# Revit family: Clevertronics_ARGO-600-LP
name_source: partatom
category: Lighting Fixtures
units: mm (PartAtom-declared; Revit-internal decimal feet)

## family parameters
Cut with Voids When Loaded = No
Host = Face
Light Source = Yes
Part Type = Normal
Room Calculation Point = No
Round Connector Dimension = Use Diameter
Shared = No

## types (5) — shared parameters
Clevertronics_240V Driver = 1330086-A - 240V Driver
Clevertronics_240V LED Strip = 8002848 - LED Strip
Clevertronics_AS2293 Classification = C0=D40 C90=D25
Clevertronics_Applicable Standards = AS/NZS3820, CISPR15, AS/NZS2293.3
Clevertronics_Battery = 3.2V 3200mAh
Clevertronics_Battery Type = Lithium Iron Phosphate
Clevertronics_Charger Method = Intelligent current limited constant voltage
Clevertronics_Construction = Polycarbonate Base and Diffuser with Captive Stainless-Steel Clips (SS301)
Clevertronics_Diffuser = Polycarbonate
Clevertronics_Driver/Ballast = LED Driver – 20w Stallion
Clevertronics_Height = 88 mm  [stored 0.288714 ft]
Clevertronics_IK Rating = IK08
Clevertronics_IP Rating = IP65
Clevertronics_Length = 655 mm  [stored 2.14895 ft]
Clevertronics_Material = Clevertronics_Plycarbonate Base
Clevertronics_Mounting = Surface mount
Clevertronics_Operating Mode = Sustained
Clevertronics_Operating Temperature = 0˚C to 40˚C
Clevertronics_Operating Voltage = 240V AC; 50Hz
Clevertronics_Replacement Battery = 1550050 - Battery
Clevertronics_Weight = 1.5 kg
Clevertronics_Width = 121 mm  [stored 0.396982 ft]
Color Filter = 16777215
Default Elevation = 6500 mm  [stored 21.3255 ft]
Dimming Lamp Color Temperature Shift = <None>
Lamp = Dual LED strip module, 3,000K warm white, 5,700K cool white, 
50,000h life [L70/B50 Ta 40°C], Ra>80
Manufacturer = Clevertronics
Photometric Web File = ARGO-600-SEN-LP_IESR_E_693-7_20200803-01.ies
Tilt Angle = -90.00°
zero-valued in all types: Clevertronics_Annotation Size

## per-type parameters (varying)
| type | Apparent Load | Clevertronics_Emergency Driver | Clevertronics_MIC Number | Clevertronics_Power Consumption | Clevertronics_Product Description | Clevertronics_Testing Node | Clevertronics_Testing System | Clevertronics_Total Lumen Output | Description | Model |
| ARGO-600-LP AUB02320450001 | 21 VA | AUM02370080001 CLIFE-PRO-CKIT-NP-335 - Driver Pack | AUB02320450001 | 21W | LP Premium ARGO 600mm LED Weatherproof Emergency Batten with Integral 
Battery and Switchable Colour, Enabled with Clevertest Plus |  | Clevertest Plus Enabled (Not activated by default) |  | LP Premium ARGO 600mm LED Weatherproof Emergency Batten with Integral 
Battery and Switchable Colour, Enabled with Clevertest Plus | ARGO-600-LP |
| ARGO-600-LP-HV  AUB02820540001 | 22 VA | AUM02870060001 CLIFE-PRO-CKIT-HV-NP-335 - Driver Pack | AUB02820540001 | 22W | LP Premium ARGO 600mm LED Weatherproof Emergency Batten with Integral 
Battery and Switchable Colour
LP Premium ARGO 600mm LED Weatherproof Emergency Batten with Integral 
Battery and Switchable Colour
LP Premium ARGO 600mm LED Weatherproof Emergency Batten with Integral 
Battery and Switchable Colour
LP Premium ARGO 600mm LED Weatherproof Emergency Batten with Integral 
Battery and Switchable Colour | 8003191 - RF Node | Zoneworks XT HIVE (RF) |  | LP Premium ARGO 600mm LED Weatherproof Emergency Batten with Integral 
Battery and Switchable Colour | ARGO-600-LP-HV |
| ARGO-600-LP-HVG  AUB02920050001 | 22 VA | AUM02970070001 CLIFE-PRO-CKIT-HVG-NP-335- Driver Pack | AUB02920050001 | 22W | Argo 600mm Weatherproof Emergency Batten, LP, Switchable Colour, 
Zoneworks XT Hive 2.4GHz | 8003560 - RF Node | Zoneworks XT HIVE (RF) | 2150lm | Argo 600mm Weatherproof Emergency Batten, LP, Switchable Colour, 
Zoneworks XT Hive 2.4GHz | ARGO-600-LP-HVG |
| ARGO-600-LP-DALI  AUB02221210002 | 22 VA | AUM02270290002 CLIFE-PRO-CKIT-DALI-NP-335 - Driver Pack | AUB02221210002 | 22W | LP Premium ARGO 600mm LED Weatherproof Emergency Batten with Integral 
Battery and Switchable Colour | 8003060 - DALI Node | DALI Registered |  | LP Premium ARGO 600mm LED Weatherproof Emergency Batten with Integral 
Battery and Switchable Colour | ARGO-600-LP-DALI |
| ARGO-600-LP-ZW  AUB02120390001 | 22 VA | AUM02170030001 CLIFE-PRO-CKIT-ZW-NP-335 - Driver Pack | AUB02120390001 | 22W | LP Premium ARGO 600mm LED Weatherproof Emergency Batten with Integral 
Battery and Switchable Colour | 8001450 - ZW Node | Zoneworks Computerised Testing | 2150lm | LP Premium ARGO 600mm LED Weatherproof Emergency Batten with Integral 
Battery and Switchable Colour | ARGO-600-LP-ZW |

note: [stored X ft] marks values corroborated as IEEE doubles in the binary element streams (Revit-internal decimal feet)

## geometry (parser evidence)
native form markers: Blend x2, Sweep x3
no freeform markers — native parametric forms only
